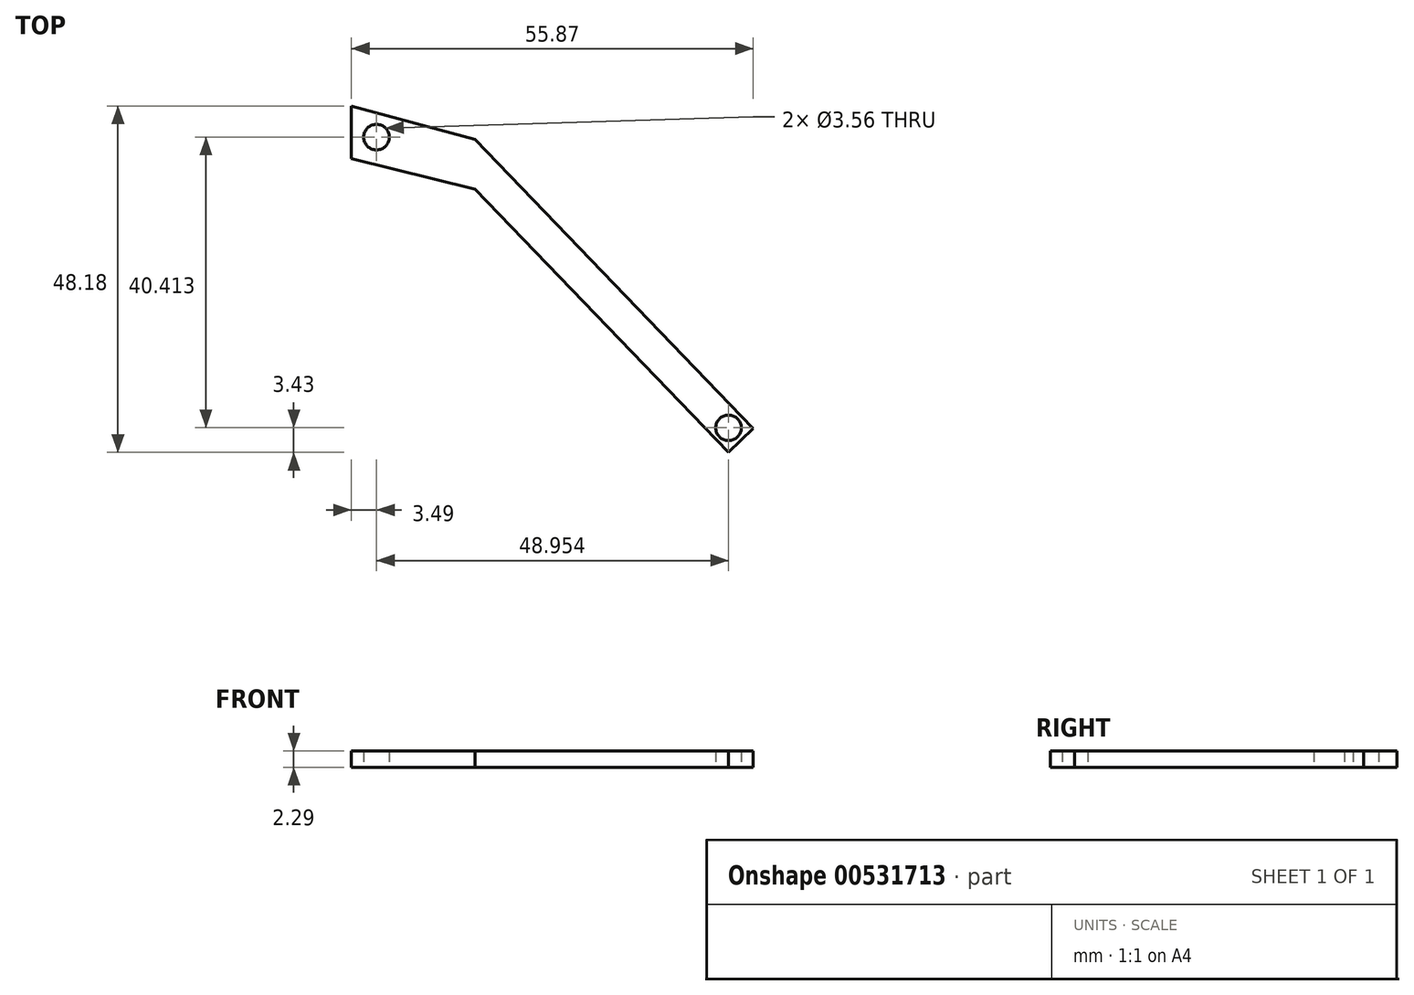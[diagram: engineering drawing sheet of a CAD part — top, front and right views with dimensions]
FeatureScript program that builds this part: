
annotation { "Feature Type Name" : "Feature", "Feature Type Description" : "" }
export const myFeature = defineFeature(function(context is Context, id is Id, definition is map)
    precondition{}
    {
        {
            var Q0;
            Q0=qCreatedBy(makeId("Top.planeOp"),FACE);
            var sketch = newSketch(context, id + "F0", { "sketchPlane" : qUnion([Q0])});
            skLineSegment(sketch, "E0", {"start": v(-38.37, 37.01) * mm, "end": v(-21.2, 32.38) * mm});
            skLineSegment(sketch, "E1", {"start": v(-21.2, 32.38) * mm, "end": v(17.5, -7.83) * mm});
            skLineSegment(sketch, "E2", {"start": v(17.5, -7.83) * mm, "end": v(14.04, -11.17) * mm});
            skLineSegment(sketch, "E3", {"start": v(14.04, -11.17) * mm, "end": v(-21.2, 25.45) * mm});
            skLineSegment(sketch, "E4", {"start": v(-21.2, 25.45) * mm, "end": v(-38.37, 29.66) * mm});
            skLineSegment(sketch, "E5", {"start": v(-38.37, 29.66) * mm, "end": v(-38.37, 37.01) * mm});
            skCircle(sketch, "E6", {"center": v(-34.88, 32.67) * mm, "radius": 1.78 * mm});
            skCircle(sketch, "E7", {"center": v(14.07, -7.74) * mm, "radius": 1.78 * mm});
            skSolve(sketch);
        }
        {
            var Q0;
            Q0=makeQuery(id+"F0.imprint","IMPRINT",FACE,{"disambiguationData":[TD([[makeQuery(id+"F0.imprint","IMPRINT",EDGE,{"derivedFrom":sQuery(id+"F0.wireOp",EDGE,"E0")}),-1.0]])]});
            extrude(context, id + "F1", {"entities" : qUnion([Q0]), "depth" : 2.3 * mm, "offsetDistance" : 25.4 * mm});
        }
    });
